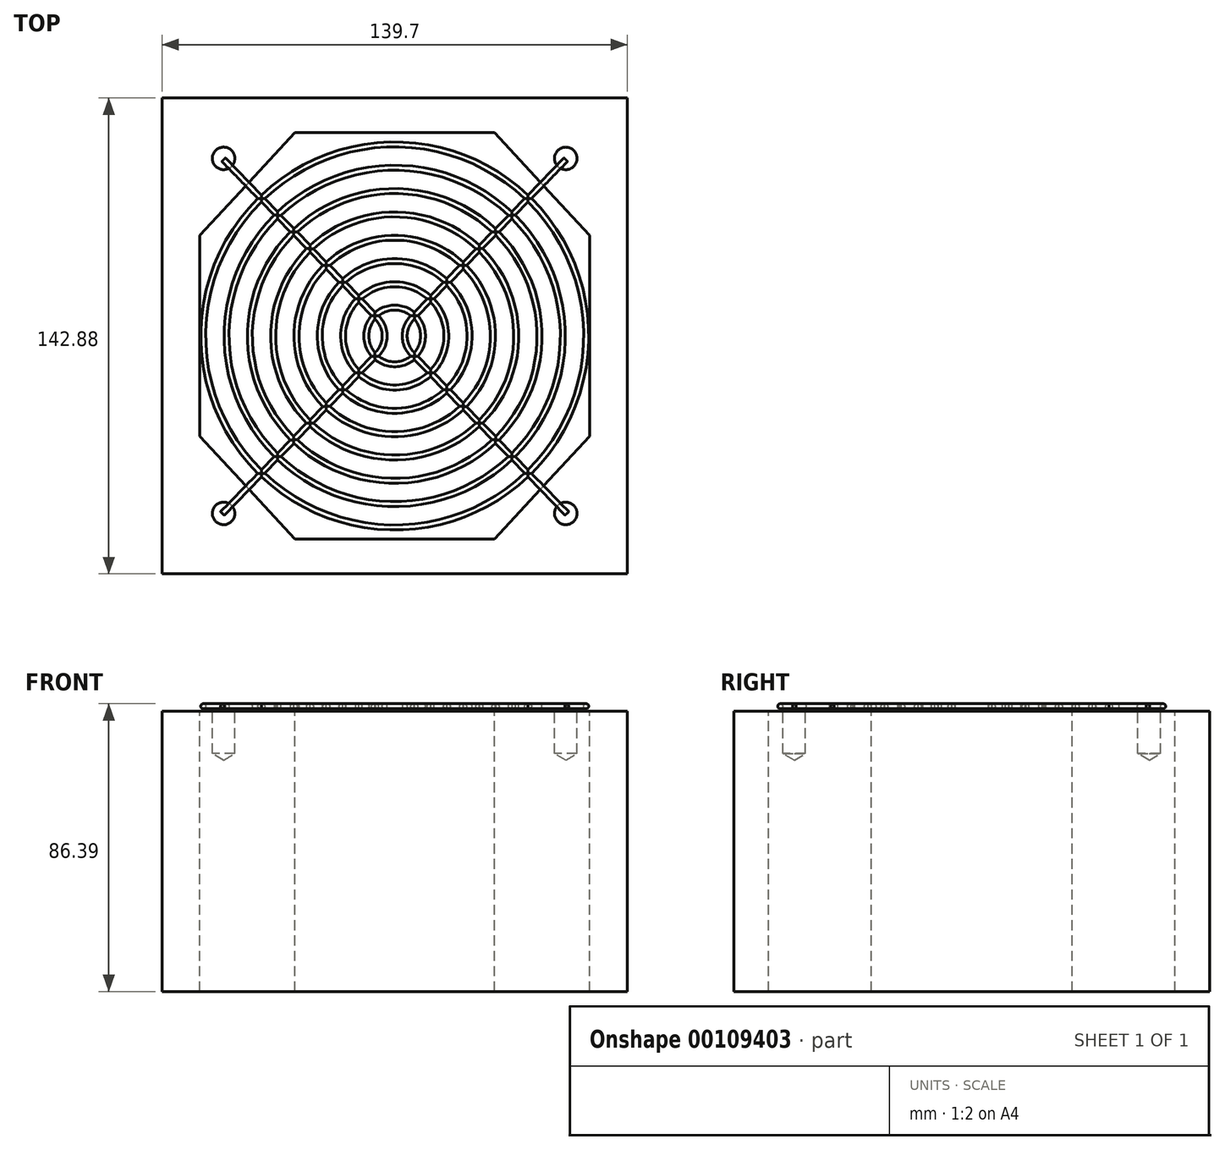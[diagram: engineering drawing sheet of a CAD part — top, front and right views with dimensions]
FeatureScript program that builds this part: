
annotation { "Feature Type Name" : "Feature", "Feature Type Description" : "" }
export const myFeature = defineFeature(function(context is Context, id is Id, definition is map)
    precondition{}
    {
        {
            var Q0;
            Q0=qCreatedBy(makeId("Top.planeOp"),FACE);
            var sketch = newSketch(context, id + "F0", { "sketchPlane" : qUnion([Q0])});
            skLineSegment(sketch, "E0.bottom", {"start": v(69.85, -71.44) * mm, "end": v(-69.85, -71.44) * mm});
            skLineSegment(sketch, "E0.top", {"start": v(69.85, 71.44) * mm, "end": v(-69.85, 71.44) * mm});
            skLineSegment(sketch, "E0.left", {"start": v(69.85, -71.44) * mm, "end": v(69.85, 71.44) * mm});
            skLineSegment(sketch, "E0.right", {"start": v(-69.85, -71.44) * mm, "end": v(-69.85, 71.44) * mm});
            skPoint(sketch, "E0.middle", {"position": v(0, 0) * mm});
            skSolve(sketch);
        }
        {
            var Q0;
            Q0 = qSketchRegion(id + "F0", true);
            extrude(context, id + "F7", {"entities" : qUnion([Q0]), "endBound" : BoundingType.SYMMETRIC, "depth" : 84.14 * mm});
        }
        {
            var Q0;
            Q0=makeQuery(id+"F7.opExtrude","CAP_FACE",FACE,{"disambiguationData":[OSD([sQuery(id+"F0.wireOp",EDGE,"E0.bottom"),sQuery(id+"F0.wireOp",EDGE,"E0.top"),sQuery(id+"F0.wireOp",EDGE,"E0.left"),sQuery(id+"F0.wireOp",EDGE,"E0.right")])],"isStart":false});
            var sketch = newSketch(context, id + "F8", { "sketchPlane" : qUnion([Q0])});
            skLineSegment(sketch, "E1", {"start": v(-30, -61.01) * mm, "end": v(30, -61.01) * mm});
            skLineSegment(sketch, "E2", {"start": v(30, -61.01) * mm, "end": v(58.5, -30.16) * mm});
            skLineSegment(sketch, "E3", {"start": v(58.5, -30.16) * mm, "end": v(58.5, 30.16) * mm});
            skLineSegment(sketch, "E4", {"start": v(58.5, 30.16) * mm, "end": v(30, 61.01) * mm});
            skLineSegment(sketch, "E5", {"start": v(30, 61.01) * mm, "end": v(-30, 61.01) * mm});
            skLineSegment(sketch, "E6", {"start": v(-30, 61.01) * mm, "end": v(-58.5, 30.16) * mm});
            skLineSegment(sketch, "E7", {"start": v(-58.5, 30.16) * mm, "end": v(-58.5, -30.16) * mm});
            skLineSegment(sketch, "E8", {"start": v(-58.5, -30.16) * mm, "end": v(-30, -61.01) * mm});
            skLineSegment(sketch, "E9", {"start": v(-69.85, 0) * mm, "end": v(69.85, 0) * mm, "construction": true});
            skLineSegment(sketch, "E10", {"start": v(0, 71.44) * mm, "end": v(0, -71.44) * mm, "construction": true});
            skLineSegment(sketch, "E11", {"start": v(-58.5, -61.01) * mm, "end": v(-44.25, -45.59) * mm, "construction": true});
            skLineSegment(sketch, "E12", {"start": v(-44.25, 45.59) * mm, "end": v(-58.5, 61.01) * mm, "construction": true});
            skPoint(sketch, "E13", {"position": v(-51.38, -53.3) * mm});
            skPoint(sketch, "E14", {"position": v(-51.38, 53.3) * mm});
            skPoint(sketch, "E15", {"position": v(51.38, -53.3) * mm});
            skPoint(sketch, "E16", {"position": v(51.38, 53.3) * mm});
            skSolve(sketch);
        }
        {
            var Q0;
            Q0 = qSketchRegion(id + "F8", true);
            extrude(context, id + "F9", {"entities" : qUnion([Q0]), "operationType" : NewBodyOperationType.REMOVE, "endBound" : BoundingType.UP_TO_NEXT, "oppositeDirection" : true, "depth" : 25.4 * mm});
        }
        {
            var Q0;
            Q0=qCreatedBy(makeId("Front.planeOp"),FACE);
            var sketch = newSketch(context, id + "F1", { "sketchPlane" : qUnion([Q0])});
            skCircle(sketch, "E17", {"center": v(8.5, 43.57) * mm, "radius": 0.75 * mm});
            skCircle(sketch, "E18", {"center": v(15.5, 43.57) * mm, "radius": 0.75 * mm});
            skCircle(sketch, "E19", {"center": v(22.5, 43.57) * mm, "radius": 0.75 * mm});
            skCircle(sketch, "E20", {"center": v(29.5, 43.57) * mm, "radius": 0.75 * mm});
            skCircle(sketch, "E21", {"center": v(36.5, 43.57) * mm, "radius": 0.75 * mm});
            skCircle(sketch, "E22", {"center": v(43.5, 43.57) * mm, "radius": 0.75 * mm});
            skCircle(sketch, "E23", {"center": v(50.5, 43.57) * mm, "radius": 0.75 * mm});
            skCircle(sketch, "E24", {"center": v(57.5, 43.57) * mm, "radius": 0.75 * mm});
            skLineSegment(sketch, "E25", {"start": v(8.5, 43.57) * mm, "end": v(57.5, 43.57) * mm, "construction": true});
            skLineSegment(sketch, "E26", {"start": v(0, 0) * mm, "end": v(0, 42.07) * mm, "construction": true});
            skSolve(sketch);
        }
        {
            var Q0;
            Q0 = qSketchRegion(id + "F1", true);
            var Q1;
            Q1=sQuery(id+"F1.wireOp",EDGE,"E26");
            revolve(context, id + "F10", {"entities" : qUnion([Q0]), "axis" : qUnion([Q1]), "revolveType" : RevolveType.FULL});
        }
        {
            var Q0;
            Q0=makeQuery(id+"F8.imprint","IMPRINT",FACE,{"disambiguationData":[TD([[makeQuery(id+"F8.imprint","IMPRINT",EDGE,{"derivedFrom":sQuery(id+"F8.wireOp",EDGE,"E1")}),-1.0]])]});
            cPlane(context, id + "F2", {"entities" : qUnion([Q0]), "cplaneType" : CPlaneType.OFFSET, "offset" : 1.5 * mm, "width" : 152.4 * mm, "height" : 152.4 * mm});
        }
        {
            var Q0;
            Q0=qCreatedBy(id+"F2.planeOp",FACE);
            var sketch = newSketch(context, id + "F3", { "sketchPlane" : qUnion([Q0])});
            skLineSegment(sketch, "E27", {"start": v(-59.22, -61.01) * mm, "end": v(-44.25, -45.59) * mm, "construction": true});
            skLineSegment(sketch, "E28", {"start": v(-44.25, 45.59) * mm, "end": v(-58.5, 60.27) * mm, "construction": true});
            skPoint(sketch, "E29.end.orphan", {"position": v(-44.25, 45.59) * mm});
            skPoint(sketch, "E30.end.orphan", {"position": v(-44.25, -45.59) * mm});
            skLineSegment(sketch, "E31", {"start": v(-51.74, -53.3) * mm, "end": v(-5.15, -5.3) * mm});
            skLineSegment(sketch, "E32", {"start": v(-5.15, 5.3) * mm, "end": v(-51.38, 52.93) * mm});
            skPoint(sketch, "E33.visualSharp", {"position": v(0, 0) * mm});
            skLineSegment(sketch, "E34", {"start": v(3, 0) * mm, "end": v(-3, 0) * mm, "construction": true});
            skArc(sketch, "E35", {"start": v(-5.15, -5.3) * mm, "mid": v(-3, 0) * mm, "end": v(-5.15, 5.3) * mm});
            skPoint(sketch, "E36", {"position": v(51.74, -53.3) * mm});
            skPoint(sketch, "E37", {"position": v(51.38, 52.93) * mm});
            skSolve(sketch);
        }
        {
            var Q0;
            Q0=sQuery(id+"F3.wireOp",VERTEX,"E31.start");
            var Q1;
            Q1=sQuery(id+"F3.wireOp",EDGE,"E27");
            cPlane(context, id + "F4", {"entities" : qUnion([Q0, Q1]), "cplaneType" : CPlaneType.LINE_POINT, "offset" : 25.4 * mm, "width" : 152.4 * mm, "height" : 152.4 * mm});
        }
        {
            var Q0;
            Q0=qCreatedBy(id+"F4.planeOp",FACE);
            var sketch = newSketch(context, id + "F11", { "sketchPlane" : qUnion([Q0])});
            skCircle(sketch, "E38", {"center": v(0, 43.57) * mm, "radius": 0.75 * mm});
            skSolve(sketch);
        }
        {
            var Q0;
            Q0 = qSketchRegion(id + "F11", true);
            var Q1;
            Q1 = qBodyType(qCreatedBy(id + "F3" ,EDGE), BodyType.WIRE);
            sweep(context, id + "F5", {"profiles" : qUnion([Q0]), "path" : qUnion([Q1])});
        }
        {
            var Q0;
            Q0=makeQuery(id+"F5.opSweep","SWEPT_BODY",BODY,{"disambiguationData":[OSD([sQuery(id+"F3.wireOp",EDGE,"E32"),sQuery(id+"F11.wireOp",EDGE,"E38")])]});
            var Q1;
            Q1=qCreatedBy(makeId("Right.planeOp"),FACE);
            mirror(context, id + "F6", {"operationType" : NewBodyOperationType.ADD, "entities" : qUnion([Q0]), "mirrorPlane" : qUnion([Q1])});
        }
        {
            var Q0;
            Q0=sQuery(id+"F8.wireOp",VERTEX,"E14");
            var Q1;
            Q1=sQuery(id+"F8.wireOp",VERTEX,"E16");
            var Q2;
            Q2=sQuery(id+"F8.wireOp",VERTEX,"E15");
            var Q3;
            Q3=sQuery(id+"F8.wireOp",VERTEX,"E13");
            var Q4;
            Q4=makeQuery(id+"F7.opExtrude","SWEPT_BODY",BODY,{"disambiguationData":[OSD([sQuery(id+"F0.wireOp",EDGE,"E0.bottom"),sQuery(id+"F0.wireOp",EDGE,"E0.top"),sQuery(id+"F0.wireOp",EDGE,"E0.left"),sQuery(id+"F0.wireOp",EDGE,"E0.right")])]});
            hole(context, id + "F12", {"style" : HoleStyle.SIMPLE, "endStyle" : HoleEndStyle.BLIND, "standardTappedOrClearance" : lookupTablePath({ "fit" : "Normal (ASME)", "standard" : "ANSI", "size" : "#6", "type" : "Tapped" }), "standardBlindInLast" : lookupTablePath({ "fit" : "Free", "standard" : "ANSI", "size" : "#6", "type" : "Tapped" }), "holeDiameter" : 6.76 * mm, "holeDepth" : 12.7 * mm, "startFromSketch" : true, "locations" : qUnion([Q0, Q1, Q2, Q3]), "scope" : qUnion([Q4])});
        }
    });
